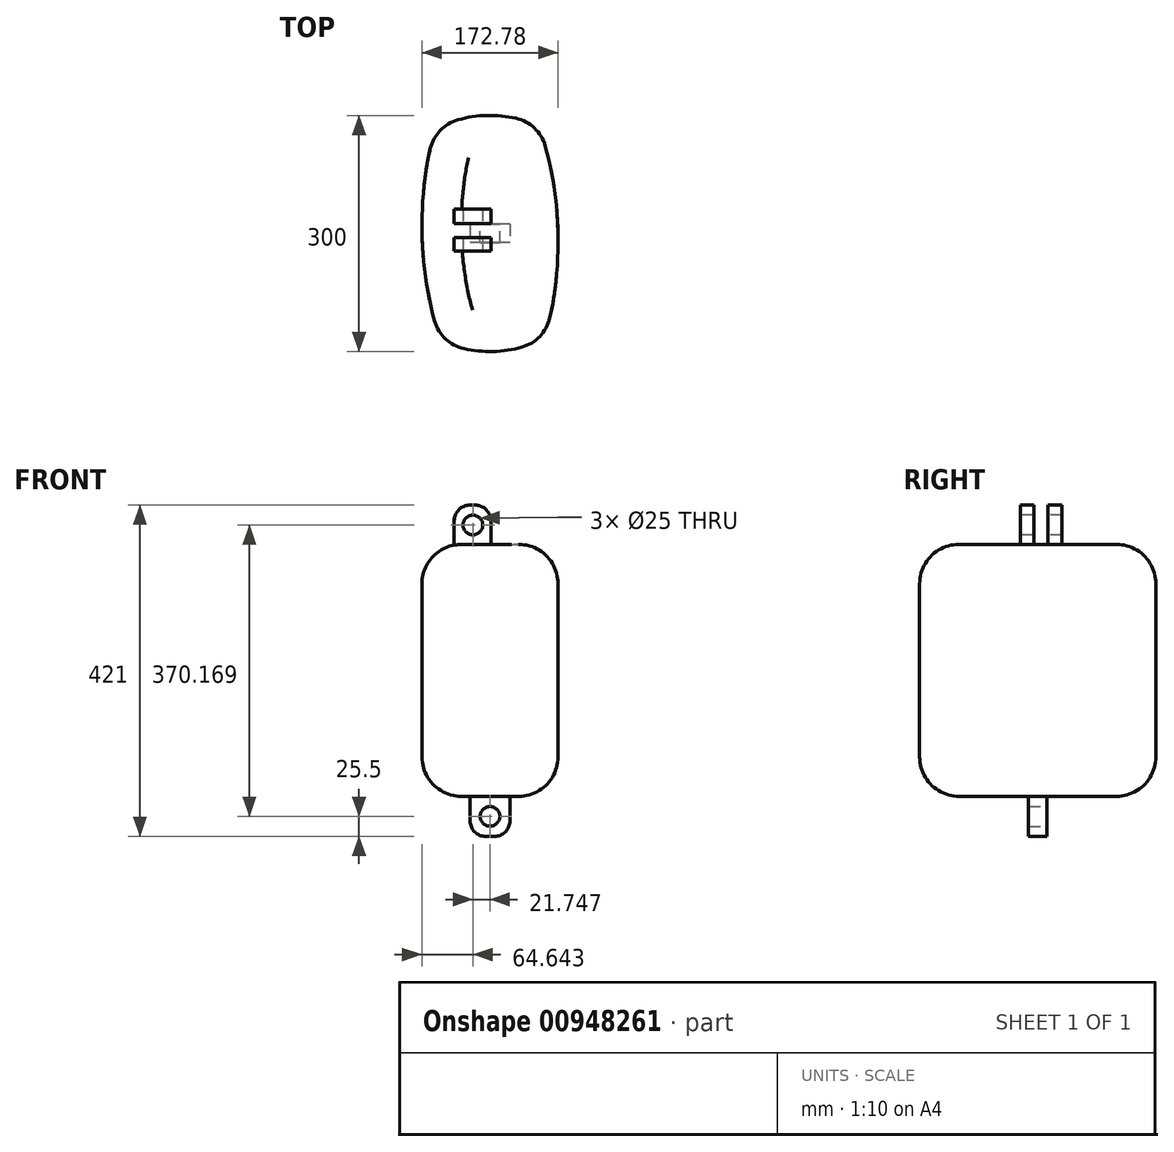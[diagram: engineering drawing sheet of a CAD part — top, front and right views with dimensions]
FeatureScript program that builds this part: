
annotation { "Feature Type Name" : "Feature", "Feature Type Description" : "" }
export const myFeature = defineFeature(function(context is Context, id is Id, definition is map)
    precondition{}
    {
        {
            var Q0;
            Q0=qCreatedBy(makeId("Top.planeOp"),FACE);
            var sketch = newSketch(context, id + "F0", { "sketchPlane" : qUnion([Q0])});
            skCircle(sketch, "E0", {"center": v(0, 0) * mm, "radius": 150 * mm});
            skEllipse(sketch, "E1", {"center": v(0, 0) * mm, "majorRadius": 206 * mm, "minorRadius": 86.25 * mm, "majorAxis": v(0.03, -1)});
            skSolve(sketch);
        }
        {
            var Q0;
            Q0=makeQuery(id+"F0.imprint","IMPRINT",FACE,{"disambiguationData":[TD([[makeQuery(id+"F0.imprint","IMPRINT",EDGE,{"derivedFrom":sQuery(id+"F0.wireOp",EDGE,"E0")}),1.0]])]});
            extrude(context, id + "F1", {"entities" : qUnion([Q0]), "depth" : 320 * mm, "offsetDistance" : 25 * mm});
        }
        {
            var Q0;
            Q0=makeQuery(id+"F1.opExtrude","CAP_FACE",FACE,{"disambiguationData":[OSD([sQuery(id+"F0.wireOp",EDGE,"E0")])],"isStart":false});
            var sketch = newSketch(context, id + "F2", { "sketchPlane" : qUnion([Q0])});
            skLineSegment(sketch, "E2.bottom", {"start": v(-45.45, -5.15) * mm, "end": v(1.05, -5.15) * mm});
            skLineSegment(sketch, "E2.top", {"start": v(-45.45, -22.14) * mm, "end": v(1.05, -22.14) * mm});
            skLineSegment(sketch, "E2.left", {"start": v(-45.45, -5.15) * mm, "end": v(-45.45, -22.14) * mm});
            skLineSegment(sketch, "E2.right", {"start": v(1.05, -5.15) * mm, "end": v(1.05, -22.14) * mm});
            skPoint(sketch, "E3.oppositeSnap0", {"position": v(1.05, -13.64) * mm});
            skLineSegment(sketch, "E3.bottom", {"start": v(-45.46, 12.75) * mm, "end": v(1.05, 12.75) * mm});
            skLineSegment(sketch, "E3.top", {"start": v(-45.46, 30.79) * mm, "end": v(1.05, 30.79) * mm});
            skLineSegment(sketch, "E3.left", {"start": v(-45.46, 12.75) * mm, "end": v(-45.46, 30.79) * mm});
            skLineSegment(sketch, "E3.right", {"start": v(1.05, 12.75) * mm, "end": v(1.05, 30.79) * mm});
            skSolve(sketch);
        }
        {
            var Q0;
            Q0=makeQuery(id+"F2.imprint","IMPRINT",FACE,{"disambiguationData":[TD([[makeQuery(id+"F2.imprint","IMPRINT",EDGE,{"derivedFrom":sQuery(id+"F2.wireOp",EDGE,"E2.bottom")}),-1.0]])]});
            var Q1;
            Q1=makeQuery(id+"F2.imprint","IMPRINT",FACE,{"disambiguationData":[TD([[makeQuery(id+"F2.imprint","IMPRINT",EDGE,{"derivedFrom":sQuery(id+"F2.wireOp",EDGE,"E3.bottom")}),1.0]])]});
            extrude(context, id + "F3", {"entities" : qUnion([Q0, Q1]), "operationType" : NewBodyOperationType.ADD, "depth" : 50 * mm, "offsetDistance" : 25 * mm});
        }
        {
            var Q0;
            Q0=makeQuery(id+"F3.opExtrude","SWEPT_FACE",FACE,{"disambiguationData":[OSD([sQuery(id+"F2.wireOp",EDGE,"E2.top")])]});
            var sketch = newSketch(context, id + "F4", { "sketchPlane" : qUnion([Q0])});
            skCircle(sketch, "E4", {"center": v(-21.75, 344.67) * mm, "radius": 12.5 * mm});
            skPoint(sketch, "E5", {"position": v(-5.44, 473.07) * mm});
            skSolve(sketch);
        }
        {
            var Q0;
            Q0=makeQuery(id+"F4.imprint","IMPRINT",FACE,{"disambiguationData":[TD([[makeQuery(id+"F4.imprint","IMPRINT",EDGE,{"derivedFrom":sQuery(id+"F4.wireOp",EDGE,"E4")}),1.0]])]});
            extrude(context, id + "F5", {"entities" : qUnion([Q0]), "operationType" : NewBodyOperationType.REMOVE, "endBound" : BoundingType.THROUGH_ALL, "oppositeDirection" : true, "depth" : 25 * mm, "offsetDistance" : 25 * mm});
        }
        {
            var Q0;
            Q0=qCreatedBy(makeId("Top.planeOp"),FACE);
            var sketch = newSketch(context, id + "F6", { "sketchPlane" : qUnion([Q0])});
            skLineSegment(sketch, "E6.bottom", {"start": v(25.3, 11.7) * mm, "end": v(-25.3, 11.7) * mm});
            skLineSegment(sketch, "E6.top", {"start": v(25.3, -11.7) * mm, "end": v(-25.3, -11.7) * mm});
            skLineSegment(sketch, "E6.left", {"start": v(25.3, 11.7) * mm, "end": v(25.3, -11.7) * mm});
            skLineSegment(sketch, "E6.right", {"start": v(-25.3, 11.7) * mm, "end": v(-25.3, -11.7) * mm});
            skPoint(sketch, "E6.middle", {"position": v(0, 0) * mm});
            skSolve(sketch);
        }
        {
            var Q0;
            Q0=makeQuery(id+"F6.imprint","IMPRINT",FACE,{"disambiguationData":[TD([[makeQuery(id+"F6.imprint","IMPRINT",EDGE,{"derivedFrom":sQuery(id+"F6.wireOp",EDGE,"E6.bottom")}),1.0]])]});
            extrude(context, id + "F7", {"entities" : qUnion([Q0]), "operationType" : NewBodyOperationType.ADD, "oppositeDirection" : true, "depth" : 51 * mm, "offsetDistance" : 25 * mm});
        }
        {
            var Q0;
            Q0=makeQuery(id+"F7.opExtrude","SWEPT_FACE",FACE,{"disambiguationData":[OSD([sQuery(id+"F6.wireOp",EDGE,"E6.bottom")])]});
            var sketch = newSketch(context, id + "F8", { "sketchPlane" : qUnion([Q0])});
            skCircle(sketch, "E7", {"center": v(0, -25.5) * mm, "radius": 12.5 * mm});
            skPoint(sketch, "E8", {"position": v(-25.3, -25.5) * mm});
            skSolve(sketch);
        }
        {
            var Q0;
            Q0=makeQuery(id+"F8.imprint","IMPRINT",FACE,{"disambiguationData":[TD([[makeQuery(id+"F8.imprint","IMPRINT",EDGE,{"derivedFrom":sQuery(id+"F8.wireOp",EDGE,"E7")}),1.0]])]});
            extrude(context, id + "F9", {"entities" : qUnion([Q0]), "operationType" : NewBodyOperationType.REMOVE, "endBound" : BoundingType.THROUGH_ALL, "oppositeDirection" : true, "depth" : 25 * mm, "offsetDistance" : 25 * mm});
        }
        {
            var Q0;
            Q0=makeQuery(id+"F3.opExtrude","CAP_EDGE",EDGE,{"disambiguationData":[OSD([sQuery(id+"F2.wireOp",EDGE,"E2.right")])],"isStart":false});
            var Q1;
            Q1=makeQuery(id+"F3.opExtrude","CAP_EDGE",EDGE,{"disambiguationData":[OSD([sQuery(id+"F2.wireOp",EDGE,"E3.right")])],"isStart":false});
            var Q2;
            Q2=makeQuery(id+"F3.opExtrude","CAP_EDGE",EDGE,{"disambiguationData":[OSD([sQuery(id+"F2.wireOp",EDGE,"E3.left")])],"isStart":false});
            var Q3;
            Q3=makeQuery(id+"F3.opExtrude","CAP_EDGE",EDGE,{"disambiguationData":[OSD([sQuery(id+"F2.wireOp",EDGE,"E2.left")])],"isStart":false});
            var Q4;
            Q4=makeQuery(id+"F7.opExtrude","CAP_EDGE",EDGE,{"disambiguationData":[OSD([sQuery(id+"F6.wireOp",EDGE,"E6.left")])],"isStart":false});
            var Q5;
            Q5=makeQuery(id+"F7.opExtrude","CAP_EDGE",EDGE,{"disambiguationData":[OSD([sQuery(id+"F6.wireOp",EDGE,"E6.right")])],"isStart":false});
            fillet(context, id + "F10", {"entities" : qUnion([Q0, Q1, Q2, Q3, Q4, Q5]), "radius" : 20 * mm, "tangentPropagation" : true, "allowEdgeOverflow" : false});
        }
        {
            var Q0;
            Q0=makeQuery(id+"F1.opExtrude","CAP_EDGE",EDGE,{"disambiguationData":[OSD([sQuery(id+"F0.wireOp",EDGE,"E0")])],"isStart":false});
            var Q1;
            Q1=makeQuery(id+"F1.opExtrude","CAP_EDGE",EDGE,{"disambiguationData":[OSD([sQuery(id+"F0.wireOp",EDGE,"E0")])],"isStart":true});
            var Q2;
            {var subQ0=sQuery(id+"F0.wireOp",EDGE,"E1");var subQ1=sQuery(id+"F0.wireOp",EDGE,"E0");Q2=makeQuery(id+"F1.opExtrude","CAP_EDGE",EDGE,{"disambiguationData":[OSD([subQ0]),TDD([makeQuery(id+"F0.imprint","IMPRINT",EDGE,{"disambiguationData":[TD([[makeQuery(id+"F0.imprint","INTERSECT",VERTEX,{"disambiguationData":[OD(1.0)],"derivedFrom":[subQ1,subQ0]}),1.0]])],"derivedFrom":subQ0})])],"isStart":false});}
            var Q3;
            {var subQ0=sQuery(id+"F0.wireOp",EDGE,"E1");var subQ1=sQuery(id+"F0.wireOp",EDGE,"E0");Q3=makeQuery(id+"F1.opExtrude","CAP_EDGE",EDGE,{"disambiguationData":[OSD([subQ0]),TDD([makeQuery(id+"F0.imprint","IMPRINT",EDGE,{"disambiguationData":[TD([[makeQuery(id+"F0.imprint","INTERSECT",VERTEX,{"disambiguationData":[OD(1.0)],"derivedFrom":[subQ1,subQ0]}),1.0]])],"derivedFrom":subQ0})])],"isStart":true});}
            var Q4;
            {var subQ0=sQuery(id+"F0.wireOp",EDGE,"E1");var subQ1=sQuery(id+"F0.wireOp",EDGE,"E0");Q4=makeQuery(id+"F1.opExtrude","SWEPT_FACE",FACE,{"disambiguationData":[OSD([subQ0]),TDD([makeQuery(id+"F0.imprint","IMPRINT",EDGE,{"disambiguationData":[TD([[makeQuery(id+"F0.imprint","INTERSECT",VERTEX,{"disambiguationData":[OD(0.0)],"derivedFrom":[subQ1,subQ0]}),-1.0]])],"derivedFrom":subQ0})])]});}
            var Q5;
            {var subQ0=sQuery(id+"F0.wireOp",EDGE,"E1");var subQ1=sQuery(id+"F0.wireOp",EDGE,"E0");Q5=makeQuery(id+"F1.opExtrude","SWEPT_FACE",FACE,{"disambiguationData":[OSD([subQ0]),TDD([makeQuery(id+"F0.imprint","IMPRINT",EDGE,{"disambiguationData":[TD([[makeQuery(id+"F0.imprint","INTERSECT",VERTEX,{"disambiguationData":[OD(1.0)],"derivedFrom":[subQ1,subQ0]}),1.0]])],"derivedFrom":subQ0})])]});}
            fillet(context, id + "F11", {"entities" : qUnion([Q0, Q1, Q2, Q3, Q4, Q5]), "radius" : 50 * mm, "tangentPropagation" : true, "defaultsChanged" : true, "vertexSettings" : [], "allowEdgeOverflow" : false});
        }
    });
